# Revit family: Showerhead-American_Standard-Modern_Rain-1660.681.002
name_source: partatom
category: Plumbing Fixtures
revit_build: Autodesk Revit 2015 (Build: 20140606_1530(x64)
units: mm (PartAtom-declared; Revit-internal decimal feet)

## types (2) — shared parameters
Assembly Code = D2010700
CW Connection = Yes
CWFU = 3
Description = 6-3/4 Inch Modern Rain Showerhead
Flow Rate = 2.5 gpm (9.5 L/min)
HW Connection = Yes
HWFU = 3
Height = 2 5/8"
Manufacturer = American Standard
Product Documentation Link = https://www.americanstandard-us.com
Product Page URL = https://www.americanstandard-us.com
Revised Date = 11/28/2019
Tempered Water Connection Diameter = 1/2"
Tempered Water Connection Radius = 1/4"
URL = http://www.americanstandard-us.com
Vent Connection = No
WFU = 4
Waste Connection = No
Width = 6 3/4"

## per-type parameters (varying)
| type | Finish | Material |
| 1660.681.002 | Brass-American Standard-002-Polished Chrome | Brass-American Standard-002-Polished Chrome |
| 1660.681.295 | Brass-American Standard-295-Brushed Nickel | Brass-American Standard-295-Brushed Nickel |

note: column(s) folded — value = type name in every type: Model

## geometry (parser evidence)
native form markers: Sweep x2
no freeform markers — native parametric forms only
